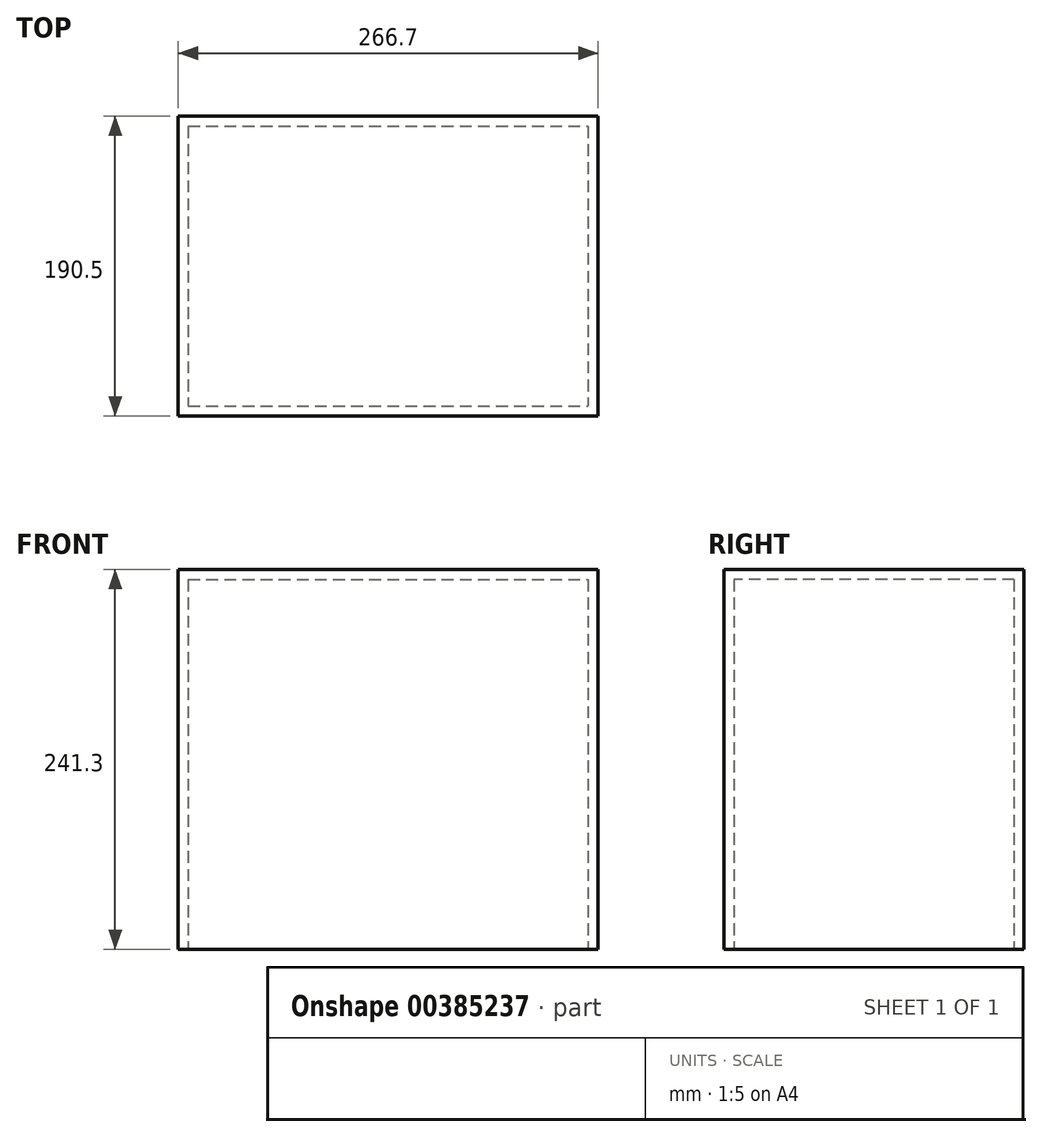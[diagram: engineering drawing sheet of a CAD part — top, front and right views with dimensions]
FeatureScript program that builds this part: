
annotation { "Feature Type Name" : "Feature", "Feature Type Description" : "" }
export const myFeature = defineFeature(function(context is Context, id is Id, definition is map)
    precondition{}
    {
        {
            var Q0;
            Q0=qCreatedBy(makeId("Top.planeOp"),FACE);
            var sketch = newSketch(context, id + "F0", { "sketchPlane" : qUnion([Q0])});
            skLineSegment(sketch, "E0.bottom", {"start": v(-115.17, 85.9) * mm, "end": v(126.13, 85.9) * mm});
            skLineSegment(sketch, "E0.top", {"start": v(-115.17, -79.2) * mm, "end": v(126.13, -79.2) * mm});
            skLineSegment(sketch, "E0.left", {"start": v(-115.17, 85.9) * mm, "end": v(-115.17, -79.2) * mm});
            skLineSegment(sketch, "E0.right", {"start": v(126.13, 85.9) * mm, "end": v(126.13, -79.2) * mm});
            skLineSegment(sketch, "E1.0", {"start": v(-121.52, 92.25) * mm, "end": v(-121.52, -85.55) * mm});
            skLineSegment(sketch, "E2.0", {"start": v(-121.52, -85.55) * mm, "end": v(132.48, -85.55) * mm});
            skLineSegment(sketch, "E3.0", {"start": v(-121.52, 92.25) * mm, "end": v(132.48, 92.25) * mm});
            skLineSegment(sketch, "E4.0", {"start": v(132.48, 92.25) * mm, "end": v(132.48, -85.55) * mm});
            skLineSegment(sketch, "E5.0", {"start": v(-127.87, 98.6) * mm, "end": v(-127.87, -91.9) * mm});
            skLineSegment(sketch, "E5.1", {"start": v(-127.87, 98.6) * mm, "end": v(138.83, 98.6) * mm});
            skLineSegment(sketch, "E5.2", {"start": v(138.83, 98.6) * mm, "end": v(138.83, -91.9) * mm});
            skLineSegment(sketch, "E5.3", {"start": v(-127.87, -91.9) * mm, "end": v(138.83, -91.9) * mm});
            skSolve(sketch);
        }
        {
            var Q0;
            Q0 = qSketchRegion(id + "F0", true);
            var Q1;
            Q1=sQuery(id+"F0.wireOp",EDGE,"E5.3");
            var Q2;
            Q2=sQuery(id+"F0.wireOp",EDGE,"E5.0");
            var Q3;
            Q3=sQuery(id+"F0.wireOp",EDGE,"E5.1");
            var Q4;
            Q4=sQuery(id+"F0.wireOp",EDGE,"E5.2");
            extrude(context, id + "F1", {"entities" : qUnion([Q0]), "surfaceEntities" : qUnion([Q1, Q2, Q3, Q4]), "depth" : 234.95 * mm});
        }
        {
            var Q0;
            Q0=makeQuery(id+"F1.opExtrude","CAP_FACE",FACE,{"disambiguationData":[OSD([sQuery(id+"F0.wireOp",EDGE,"E1.0"),sQuery(id+"F0.wireOp",EDGE,"E2.0"),sQuery(id+"F0.wireOp",EDGE,"E3.0"),sQuery(id+"F0.wireOp",EDGE,"E4.0"),sQuery(id+"F0.wireOp",EDGE,"E5.0"),sQuery(id+"F0.wireOp",EDGE,"E5.1"),sQuery(id+"F0.wireOp",EDGE,"E5.2"),sQuery(id+"F0.wireOp",EDGE,"E5.3")])],"isStart":false});
            var sketch = newSketch(context, id + "F2", { "sketchPlane" : qUnion([Q0])});
            skLineSegment(sketch, "E6.bottom", {"start": v(-127.87, 98.6) * mm, "end": v(138.83, 98.6) * mm});
            skLineSegment(sketch, "E6.top", {"start": v(-127.87, -91.9) * mm, "end": v(138.83, -91.9) * mm});
            skLineSegment(sketch, "E6.left", {"start": v(-127.87, 98.6) * mm, "end": v(-127.87, -91.9) * mm});
            skLineSegment(sketch, "E6.right", {"start": v(138.83, 98.6) * mm, "end": v(138.83, -91.9) * mm});
            skSolve(sketch);
        }
        {
            var Q0;
            Q0 = qSketchRegion(id + "F2", true);
            extrude(context, id + "F3", {"entities" : qUnion([Q0]), "operationType" : NewBodyOperationType.ADD, "depth" : 6.35 * mm});
        }
    });
